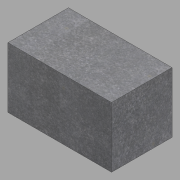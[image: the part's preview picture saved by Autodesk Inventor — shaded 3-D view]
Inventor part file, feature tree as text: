
AUTODESK INVENTOR PART (.ipt)
format: ipt  version: 2022.1 (Build 261234020, 234B)  size: 128,000 bytes
history: native  units: in
note: dims shown in document units (in); Inventor stores cm internally (conversion verified against a paired STEP export)
features: other x1, extrude x1, sketch x1
ambient origin geometry x8: Origin, YZ Plane, XZ Plane, XY Plane, X Axis, Y Axis, Z Axis, Center Point
bodies: Solid1 (feature_tree)
feature tree (3):
  other  "1st"
  extrude  "Extrusion1"  Depth=35.0in
  sketch  "Sketch1"  dims[d0=60.0in d1=35.0in d2=35.0in d3=0.0in]
